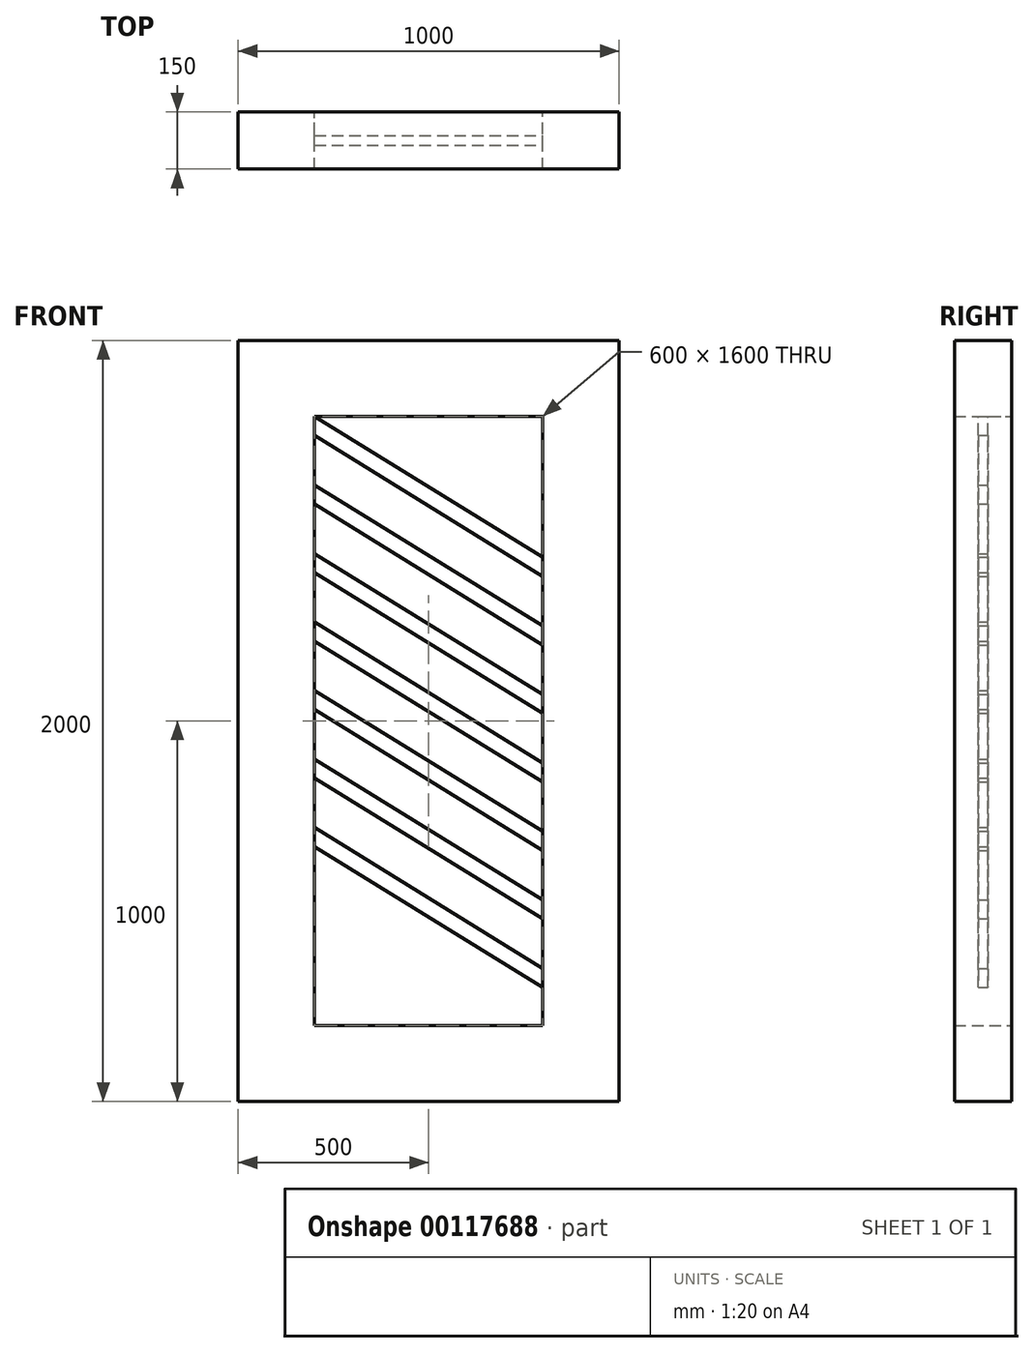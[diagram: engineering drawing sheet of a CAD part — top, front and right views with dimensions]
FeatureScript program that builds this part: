
annotation { "Feature Type Name" : "Feature", "Feature Type Description" : "" }
export const myFeature = defineFeature(function(context is Context, id is Id, definition is map)
    precondition{}
    {
        {
            var Q0;
            Q0=qCreatedBy(makeId("Front.planeOp"),FACE);
            var sketch = newSketch(context, id + "F0", { "sketchPlane" : qUnion([Q0])});
            skLineSegment(sketch, "E0.bottom", {"start": v(0, 0) * mm, "end": v(1000, 0) * mm});
            skLineSegment(sketch, "E0.top", {"start": v(0, 2000) * mm, "end": v(1000, 2000) * mm});
            skLineSegment(sketch, "E0.left", {"start": v(0, 0) * mm, "end": v(0, 2000) * mm});
            skLineSegment(sketch, "E0.right", {"start": v(1000, 0) * mm, "end": v(1000, 2000) * mm});
            skLineSegment(sketch, "E1.bottom", {"start": v(200, 200) * mm, "end": v(800, 200) * mm});
            skLineSegment(sketch, "E1.top", {"start": v(200, 1800) * mm, "end": v(800, 1800) * mm});
            skLineSegment(sketch, "E1.left", {"start": v(200, 200) * mm, "end": v(200, 1800) * mm});
            skLineSegment(sketch, "E1.right", {"start": v(800, 200) * mm, "end": v(800, 1800) * mm});
            skSolve(sketch);
        }
        {
            var Q0;
            Q0=makeQuery(id+"F0.imprint","IMPRINT",FACE,{"disambiguationData":[TD([[makeQuery(id+"F0.imprint","IMPRINT",EDGE,{"derivedFrom":sQuery(id+"F0.wireOp",EDGE,"E0.bottom")}),1.0]])]});
            extrude(context, id + "F1", {"entities" : qUnion([Q0]), "endBound" : BoundingType.SYMMETRIC, "depth" : 150 * mm});
        }
        {
            var Q0;
            Q0=qCreatedBy(makeId("Front.planeOp"),FACE);
            var sketch = newSketch(context, id + "F2", { "sketchPlane" : qUnion([Q0])});
            skLineSegment(sketch, "E2.0", {"start": v(200, 200) * mm, "end": v(200, 1800) * mm});
            skLineSegment(sketch, "E2.1", {"start": v(200, 1800) * mm, "end": v(800, 1800) * mm});
            skLineSegment(sketch, "E2.2", {"start": v(800, 200) * mm, "end": v(800, 1800) * mm});
            skLineSegment(sketch, "E2.3", {"start": v(200, 200) * mm, "end": v(800, 200) * mm});
            skLineSegment(sketch, "E3", {"start": v(200, 1750) * mm, "end": v(800, 1380) * mm});
            skLineSegment(sketch, "E4", {"start": v(800, 1430) * mm, "end": v(800, 1380) * mm});
            skLineSegment(sketch, "E5", {"start": v(800, 1430) * mm, "end": v(200, 1800) * mm});
            skLineSegment(sketch, "E6", {"start": v(200, 1750) * mm, "end": v(200, 1800) * mm});
            skLineSegment(sketch, "E7.1.0.0", {"start": v(200, 1570) * mm, "end": v(800, 1200) * mm});
            skLineSegment(sketch, "E7.1.0.1", {"start": v(800, 1250) * mm, "end": v(800, 1200) * mm});
            skLineSegment(sketch, "E7.1.0.2", {"start": v(200, 1570) * mm, "end": v(200, 1620) * mm});
            skLineSegment(sketch, "E7.1.0.3", {"start": v(800, 1250) * mm, "end": v(200, 1620) * mm});
            skLineSegment(sketch, "E7.2.0.0", {"start": v(200, 1390) * mm, "end": v(800, 1020) * mm});
            skLineSegment(sketch, "E7.2.0.1", {"start": v(800, 1070) * mm, "end": v(800, 1020) * mm});
            skLineSegment(sketch, "E7.2.0.2", {"start": v(200, 1390) * mm, "end": v(200, 1440) * mm});
            skLineSegment(sketch, "E7.2.0.3", {"start": v(800, 1070) * mm, "end": v(200, 1440) * mm});
            skLineSegment(sketch, "E7.3.0.0", {"start": v(200, 1210) * mm, "end": v(800, 840) * mm});
            skLineSegment(sketch, "E7.3.0.1", {"start": v(800, 890) * mm, "end": v(800, 840) * mm});
            skLineSegment(sketch, "E7.3.0.2", {"start": v(200, 1210) * mm, "end": v(200, 1260) * mm});
            skLineSegment(sketch, "E7.3.0.3", {"start": v(800, 890) * mm, "end": v(200, 1260) * mm});
            skLineSegment(sketch, "E7.4.0.0", {"start": v(200, 1030) * mm, "end": v(800, 660) * mm});
            skLineSegment(sketch, "E7.4.0.1", {"start": v(800, 710) * mm, "end": v(800, 660) * mm});
            skLineSegment(sketch, "E7.4.0.2", {"start": v(200, 1030) * mm, "end": v(200, 1080) * mm});
            skLineSegment(sketch, "E7.4.0.3", {"start": v(800, 710) * mm, "end": v(200, 1080) * mm});
            skLineSegment(sketch, "E7.direction1", {"start": v(200, 1800) * mm, "end": v(200, 1620) * mm, "construction": true});
            skLineSegment(sketch, "E8.0.5.0", {"start": v(200, 850) * mm, "end": v(800, 480) * mm});
            skLineSegment(sketch, "E8.3.5.0", {"start": v(800, 530) * mm, "end": v(800, 480) * mm});
            skLineSegment(sketch, "E8.6.5.0", {"start": v(200, 850) * mm, "end": v(200, 900) * mm});
            skLineSegment(sketch, "E8.9.5.0", {"start": v(800, 530) * mm, "end": v(200, 900) * mm});
            skLineSegment(sketch, "E8.0.6.0", {"start": v(200, 670) * mm, "end": v(800, 300) * mm});
            skLineSegment(sketch, "E8.3.6.0", {"start": v(800, 350) * mm, "end": v(800, 300) * mm});
            skLineSegment(sketch, "E8.6.6.0", {"start": v(200, 670) * mm, "end": v(200, 720) * mm});
            skLineSegment(sketch, "E8.9.6.0", {"start": v(800, 350) * mm, "end": v(200, 720) * mm});
            skSolve(sketch);
        }
        {
            var Q0;
            Q0=makeQuery(id+"F2.imprint","IMPRINT",FACE,{"disambiguationData":[TD([[makeQuery(id+"F2.imprint","IMPRINT",EDGE,{"derivedFrom":sQuery(id+"F2.wireOp",EDGE,"E3")}),1.0]])]});
            var Q1;
            Q1=makeQuery(id+"F2.imprint","IMPRINT",FACE,{"disambiguationData":[TD([[makeQuery(id+"F2.imprint","IMPRINT",EDGE,{"derivedFrom":sQuery(id+"F2.wireOp",EDGE,"E7.1.0.0")}),1.0]])]});
            var Q2;
            Q2=makeQuery(id+"F2.imprint","IMPRINT",FACE,{"disambiguationData":[TD([[makeQuery(id+"F2.imprint","IMPRINT",EDGE,{"derivedFrom":sQuery(id+"F2.wireOp",EDGE,"E7.2.0.0")}),1.0]])]});
            var Q3;
            Q3=makeQuery(id+"F2.imprint","IMPRINT",FACE,{"disambiguationData":[TD([[makeQuery(id+"F2.imprint","IMPRINT",EDGE,{"derivedFrom":sQuery(id+"F2.wireOp",EDGE,"E7.3.0.0")}),1.0]])]});
            var Q4;
            Q4=makeQuery(id+"F2.imprint","IMPRINT",FACE,{"disambiguationData":[TD([[makeQuery(id+"F2.imprint","IMPRINT",EDGE,{"derivedFrom":sQuery(id+"F2.wireOp",EDGE,"E7.4.0.0")}),1.0]])]});
            var Q5;
            Q5=makeQuery(id+"F2.imprint","IMPRINT",FACE,{"disambiguationData":[TD([[makeQuery(id+"F2.imprint","IMPRINT",EDGE,{"derivedFrom":sQuery(id+"F2.wireOp",EDGE,"E8.0.5.0")}),1.0]])]});
            var Q6;
            Q6=makeQuery(id+"F2.imprint","IMPRINT",FACE,{"disambiguationData":[TD([[makeQuery(id+"F2.imprint","IMPRINT",EDGE,{"derivedFrom":sQuery(id+"F2.wireOp",EDGE,"E8.0.6.0")}),1.0]])]});
            extrude(context, id + "F3", {"entities" : qUnion([Q0, Q1, Q2, Q3, Q4, Q5, Q6]), "operationType" : NewBodyOperationType.ADD, "endBound" : BoundingType.SYMMETRIC, "depth" : 25 * mm});
        }
    });
